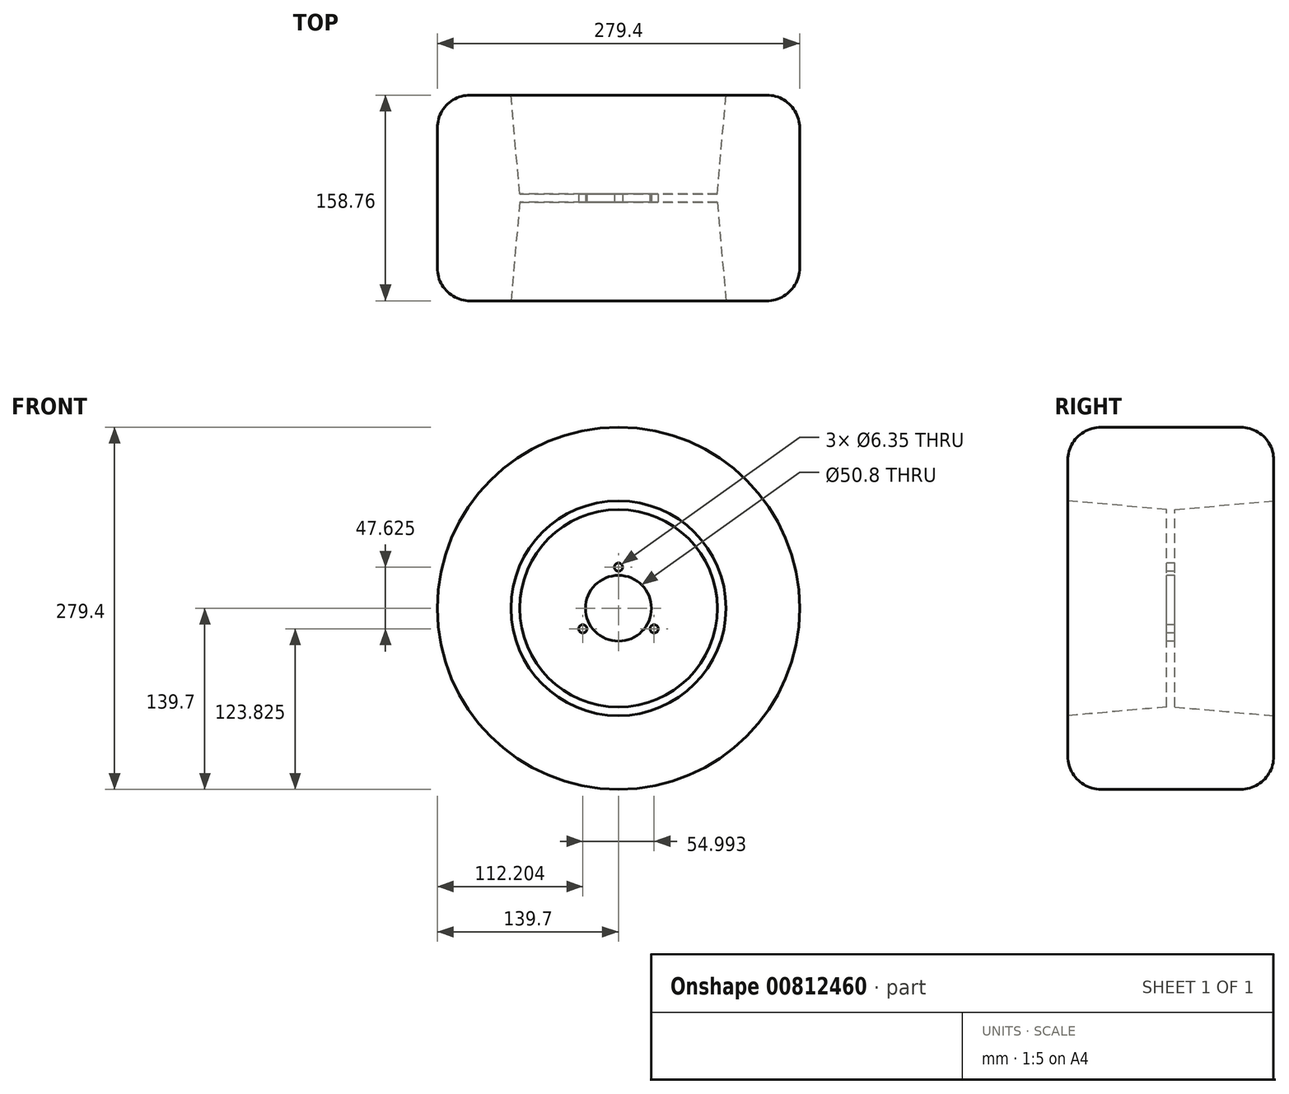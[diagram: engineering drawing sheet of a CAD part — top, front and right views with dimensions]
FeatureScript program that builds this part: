
annotation { "Feature Type Name" : "Feature", "Feature Type Description" : "" }
export const myFeature = defineFeature(function(context is Context, id is Id, definition is map)
    precondition{}
    {
        {
            var Q0;
            Q0=qCreatedBy(makeId("Top.planeOp"),FACE);
            var sketch = newSketch(context, id + "F0", { "sketchPlane" : qUnion([Q0])});
            skLineSegment(sketch, "E0", {"start": v(0, 0) * mm, "end": v(0, 3.18) * mm});
            skLineSegment(sketch, "E1", {"start": v(0, 3.18) * mm, "end": v(76.2, 3.18) * mm});
            skLineSegment(sketch, "E2", {"start": v(76.2, 3.17) * mm, "end": v(82.87, 79.38) * mm});
            skLineSegment(sketch, "E3", {"start": v(82.87, 79.38) * mm, "end": v(139.7, 79.38) * mm});
            skLineSegment(sketch, "E4", {"start": v(139.7, 79.38) * mm, "end": v(139.7, 0) * mm});
            skLineSegment(sketch, "E5.MirrorCS", {"start": v(0, 0) * mm, "end": v(0, -3.18) * mm});
            skLineSegment(sketch, "E6.MirrorCS", {"start": v(82.87, -79.38) * mm, "end": v(139.7, -79.38) * mm});
            skLineSegment(sketch, "E7.MirrorCS", {"start": v(0, -3.18) * mm, "end": v(76.2, -3.18) * mm});
            skLineSegment(sketch, "E8.MirrorCS", {"start": v(76.2, -3.17) * mm, "end": v(82.87, -79.38) * mm});
            skLineSegment(sketch, "E9.MirrorCS", {"start": v(139.7, -79.38) * mm, "end": v(139.7, 0) * mm});
            skSolve(sketch);
        }
        {
            var Q0;
            Q0=makeQuery(id+"F0.imprint","IMPRINT",FACE,{"disambiguationData":[TD([[makeQuery(id+"F0.imprint","IMPRINT",EDGE,{"derivedFrom":sQuery(id+"F0.wireOp",EDGE,"E0")}),-1.0]])]});
            var Q1;
            Q1=sQuery(id+"F0.wireOp",EDGE,"E0");
            revolve(context, id + "F1", {"surfaceOperationType" : NewSurfaceOperationType.NEW, "entities" : qUnion([Q0]), "axis" : qUnion([Q1]), "revolveType" : RevolveType.FULL});
        }
        {
            var Q0;
            Q0=makeQuery(id+"F1.opRevolve","SWEPT_EDGE",EDGE,{"disambiguationData":[OSD([sQuery(id+"F0.wireOp",EDGE,"E6.MirrorCS"),sQuery(id+"F0.wireOp",EDGE,"E9.MirrorCS")])]});
            var Q1;
            Q1=makeQuery(id+"F1.opRevolve","SWEPT_EDGE",EDGE,{"disambiguationData":[OSD([sQuery(id+"F0.wireOp",EDGE,"E3"),sQuery(id+"F0.wireOp",EDGE,"E4")])]});
            fillet(context, id + "F2", {"entities" : qUnion([Q0, Q1]), "radius" : 25.4 * mm, "tangentPropagation" : true, "allowEdgeOverflow" : false});
        }
        {
            var Q0;
            Q0=makeQuery(id+"F1.opRevolve","SWEPT_FACE",FACE,{"disambiguationData":[OSD([sQuery(id+"F0.wireOp",EDGE,"E7.MirrorCS")])]});
            var sketch = newSketch(context, id + "F3", { "sketchPlane" : qUnion([Q0])});
            skCircle(sketch, "E10", {"center": v(0, 0) * mm, "radius": 25.4 * mm});
            skCircle(sketch, "E11", {"center": v(0, 31.75) * mm, "radius": 3.18 * mm});
            skCircle(sketch, "E12.1.0", {"center": v(-27.5, -15.87) * mm, "radius": 3.18 * mm});
            skCircle(sketch, "E12.2.0", {"center": v(27.5, -15.88) * mm, "radius": 3.18 * mm});
            skSolve(sketch);
        }
        {
            var Q0;
            Q0=makeQuery(id+"F3.imprint","IMPRINT",FACE,{"disambiguationData":[TD([[makeQuery(id+"F3.imprint","IMPRINT",EDGE,{"derivedFrom":sQuery(id+"F3.wireOp",EDGE,"E10")}),1.0]])]});
            var Q1;
            Q1=makeQuery(id+"F3.imprint","IMPRINT",FACE,{"disambiguationData":[TD([[makeQuery(id+"F3.imprint","IMPRINT",EDGE,{"derivedFrom":sQuery(id+"F3.wireOp",EDGE,"E11")}),1.0]])]});
            var Q2;
            Q2=makeQuery(id+"F3.imprint","IMPRINT",FACE,{"disambiguationData":[TD([[makeQuery(id+"F3.imprint","IMPRINT",EDGE,{"derivedFrom":sQuery(id+"F3.wireOp",EDGE,"E12.1.0")}),1.0]])]});
            var Q3;
            Q3=makeQuery(id+"F3.imprint","IMPRINT",FACE,{"disambiguationData":[TD([[makeQuery(id+"F3.imprint","IMPRINT",EDGE,{"derivedFrom":sQuery(id+"F3.wireOp",EDGE,"E12.2.0")}),1.0]])]});
            extrude(context, id + "F4", {"entities" : qUnion([Q0, Q1, Q2, Q3]), "operationType" : NewBodyOperationType.REMOVE, "endBound" : BoundingType.THROUGH_ALL, "oppositeDirection" : true, "depth" : 25.4 * mm, "offsetDistance" : 25.4 * mm});
        }
    });
